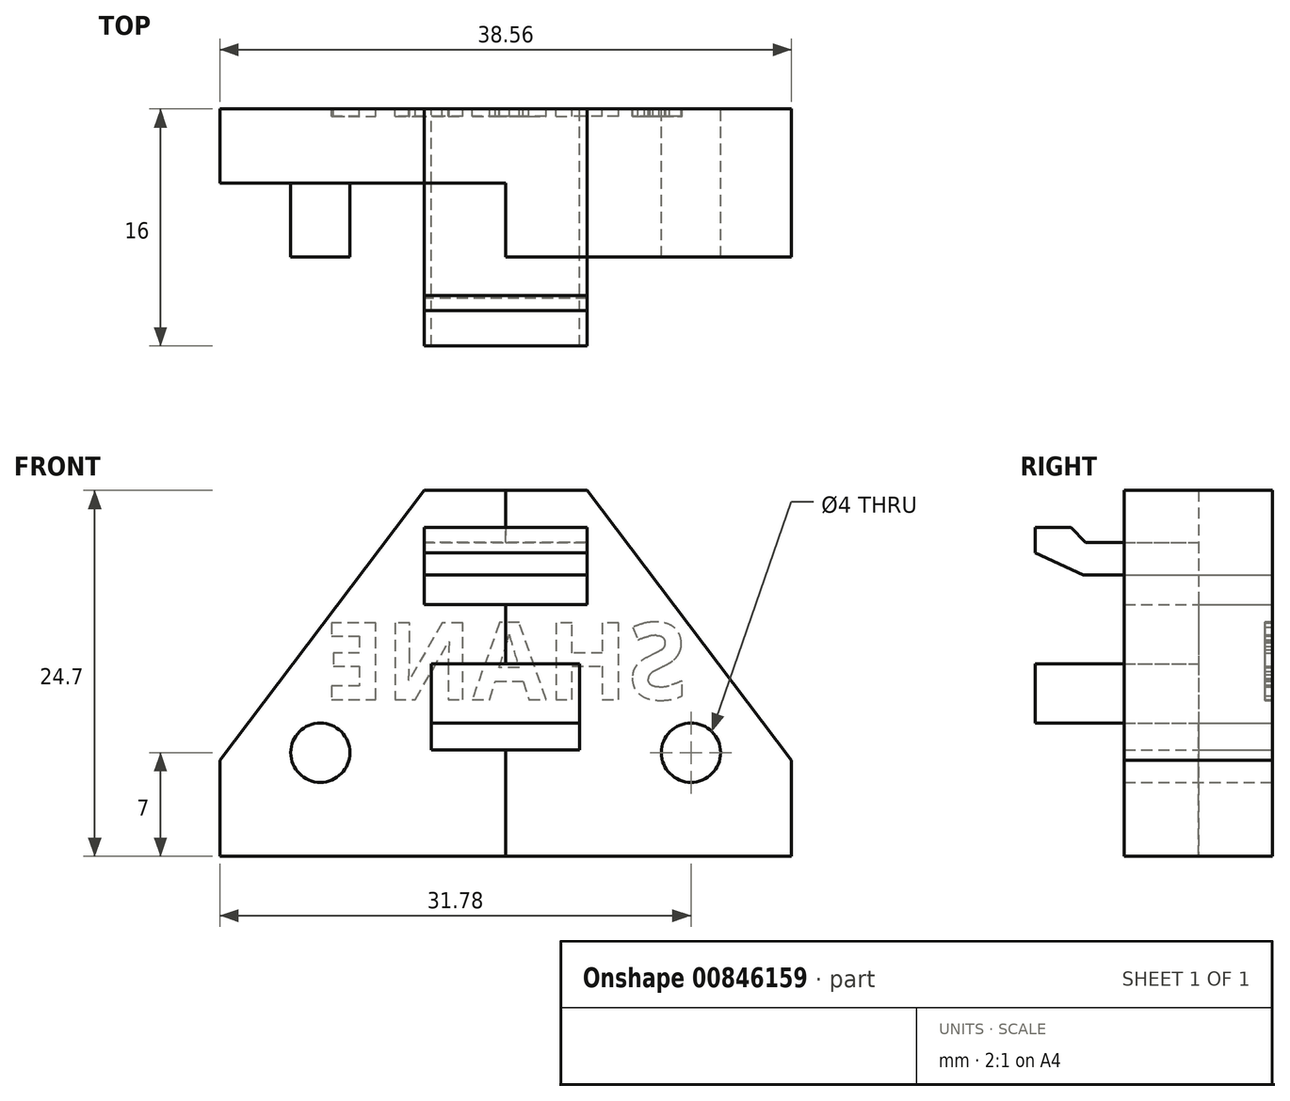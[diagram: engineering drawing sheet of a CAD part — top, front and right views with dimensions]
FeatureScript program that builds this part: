
annotation { "Feature Type Name" : "Feature", "Feature Type Description" : "" }
export const myFeature = defineFeature(function(context is Context, id is Id, definition is map)
    precondition{}
    {
        {
            var Q0;
            Q0=qCreatedBy(makeId("Front.planeOp"),FACE);
            var sketch = newSketch(context, id + "F0", { "sketchPlane" : qUnion([Q0])});
            skPoint(sketch, "E0", {"position": v(0, 0) * mm});
            skPoint(sketch, "E1", {"position": v(0, -2) * mm});
            skPoint(sketch, "E2", {"position": v(-12.5, -2) * mm});
            skLineSegment(sketch, "E3", {"start": v(0, 0) * mm, "end": v(0, 10) * mm, "construction": true});
            skCircle(sketch, "E4", {"center": v(-12.5, -2) * mm, "radius": 2 * mm});
            skLineSegment(sketch, "E5.bottom", {"start": v(-5, 0) * mm, "end": v(5, 0) * mm});
            skLineSegment(sketch, "E5.top", {"start": v(-5, 4) * mm, "end": v(5, 4) * mm});
            skLineSegment(sketch, "E5.left", {"start": v(-5, 0) * mm, "end": v(-5, 4) * mm});
            skLineSegment(sketch, "E5.right", {"start": v(5, 0) * mm, "end": v(5, 4) * mm});
            skPoint(sketch, "E5.middle", {"position": v(0, 2) * mm});
            skLineSegment(sketch, "E6.bottom", {"start": v(-5.5, 10) * mm, "end": v(5.5, 10) * mm});
            skLineSegment(sketch, "E6.top", {"start": v(-5.5, 12.2) * mm, "end": v(5.5, 12.2) * mm});
            skLineSegment(sketch, "E6.left", {"start": v(-5.5, 10) * mm, "end": v(-5.5, 12.2) * mm});
            skLineSegment(sketch, "E6.right", {"start": v(5.5, 10) * mm, "end": v(5.5, 12.2) * mm});
            skPoint(sketch, "E6.middle", {"position": v(0, 11.1) * mm});
            skLineSegment(sketch, "E7.top", {"start": v(-5, -1.8) * mm, "end": v(5, -1.8) * mm});
            skLineSegment(sketch, "E7.left", {"start": v(-5, 0) * mm, "end": v(-5, -1.8) * mm});
            skLineSegment(sketch, "E7.right", {"start": v(5, 0) * mm, "end": v(5, -1.8) * mm});
            skLineSegment(sketch, "E8.top", {"start": v(-5.5, 8) * mm, "end": v(5.5, 8) * mm});
            skLineSegment(sketch, "E8.left", {"start": v(-5.5, 10) * mm, "end": v(-5.5, 8) * mm});
            skLineSegment(sketch, "E8.right", {"start": v(5.5, 10) * mm, "end": v(5.5, 8) * mm});
            skLineSegment(sketch, "E9.bottom", {"start": v(0, -9) * mm, "end": v(-19.28, -9) * mm});
            skLineSegment(sketch, "E9.top", {"start": v(0, 15.7) * mm, "end": v(-19.28, 15.7) * mm});
            skLineSegment(sketch, "E9.left", {"start": v(0, -9) * mm, "end": v(0, 15.7) * mm});
            skLineSegment(sketch, "E9.right", {"start": v(-19.28, -9) * mm, "end": v(-19.28, 15.7) * mm});
            skLineSegment(sketch, "E10", {"start": v(-5.5, 15.7) * mm, "end": v(-19.28, -2.5) * mm});
            skCircle(sketch, "E11.MirrorC", {"center": v(12.5, -2) * mm, "radius": 2 * mm});
            skLineSegment(sketch, "E12.MirrorCS", {"start": v(5.5, 15.7) * mm, "end": v(19.28, -2.5) * mm});
            skLineSegment(sketch, "E13.MirrorCS", {"start": v(19.28, -9) * mm, "end": v(19.28, 15.7) * mm});
            skLineSegment(sketch, "E14.MirrorCS", {"start": v(0, -9) * mm, "end": v(19.28, -9) * mm});
            skLineSegment(sketch, "E15.MirrorCS", {"start": v(0, 15.7) * mm, "end": v(19.28, 15.7) * mm});
            skSolve(sketch);
        }
        {
            var Q0;
            Q0=makeQuery(id+"F0.imprint","IMPRINT",FACE,{"disambiguationData":[TD([[makeQuery(id+"F0.imprint","IMPRINT",EDGE,{"derivedFrom":sQuery(id+"F0.wireOp",EDGE,"E4")}),-1.0]])]});
            var Q1;
            {var subQ5=sQuery(id+"F0.wireOp",EDGE,"E5.right");Q1=makeQuery(id+"F0.imprint","IMPRINT",FACE,{"disambiguationData":[TD([[makeQuery(id+"F0.imprint","IMPRINT",EDGE,{"derivedFrom":subQ5}),-1.0]])]});}
            extrude(context, id + "F1", {"entities" : qUnion([Q0, Q1]), "depth" : 5 * mm, "offsetDistance" : 25 * mm});
        }
        {
            var Q0;
            Q0=makeQuery(id+"F0.imprint","IMPRINT",FACE,{"disambiguationData":[TD([[makeQuery(id+"F0.imprint","IMPRINT",EDGE,{"derivedFrom":sQuery(id+"F0.wireOp",EDGE,"E4")}),1.0]])]});
            var Q1;
            Q1=makeQuery(id+"F0.imprint","IMPRINT",FACE,{"disambiguationData":[TD([[makeQuery(id+"F0.imprint","IMPRINT",EDGE,{"derivedFrom":sQuery(id+"F0.wireOp",EDGE,"E11.MirrorC")}),-1.0]])]});
            extrude(context, id + "F2", {"entities" : qUnion([Q0, Q1]), "operationType" : NewBodyOperationType.ADD, "depth" : 10 * mm, "offsetDistance" : 25 * mm});
        }
        {
            var Q0;
            {var subQ0=sQuery(id+"F0.wireOp",EDGE,"E5.right");Q0=makeQuery(id+"F0.imprint","IMPRINT",FACE,{"disambiguationData":[TD([[makeQuery(id+"F0.imprint","IMPRINT",EDGE,{"derivedFrom":subQ0}),1.0]])]});}
            var Q1;
            {var subQ0=sQuery(id+"F0.wireOp",EDGE,"E5.left");Q1=makeQuery(id+"F0.imprint","IMPRINT",FACE,{"disambiguationData":[TD([[makeQuery(id+"F0.imprint","IMPRINT",EDGE,{"derivedFrom":subQ0}),-1.0]])]});}
            var Q2;
            {var subQ0=sQuery(id+"F0.wireOp",EDGE,"E6.left");Q2=makeQuery(id+"F0.imprint","IMPRINT",FACE,{"disambiguationData":[TD([[makeQuery(id+"F0.imprint","IMPRINT",EDGE,{"derivedFrom":subQ0}),-1.0]])]});}
            var Q3;
            {var subQ0=sQuery(id+"F0.wireOp",EDGE,"E6.right");Q3=makeQuery(id+"F0.imprint","IMPRINT",FACE,{"disambiguationData":[TD([[makeQuery(id+"F0.imprint","IMPRINT",EDGE,{"derivedFrom":subQ0}),1.0]])]});}
            extrude(context, id + "F3", {"entities" : qUnion([Q0, Q1, Q2, Q3]), "operationType" : NewBodyOperationType.ADD, "depth" : 16 * mm, "offsetDistance" : 25 * mm});
        }
        {
            var Q0;
            Q0=makeQuery(id+"F3.opExtrude","SWEPT_FACE",FACE,{"disambiguationData":[OSD([sQuery(id+"F0.wireOp",EDGE,"E6.top")])]});
            var sketch = newSketch(context, id + "F4", { "sketchPlane" : qUnion([Q0])});
            skLineSegment(sketch, "E16.bottom", {"start": v(5.5, -16) * mm, "end": v(-5.5, -16) * mm});
            skLineSegment(sketch, "E16.top", {"start": v(5.5, -12.6) * mm, "end": v(-5.5, -12.6) * mm});
            skLineSegment(sketch, "E16.left", {"start": v(5.5, -16) * mm, "end": v(5.5, -12.6) * mm});
            skLineSegment(sketch, "E16.right", {"start": v(-5.5, -16) * mm, "end": v(-5.5, -12.6) * mm});
            skSolve(sketch);
        }
        {
            var Q0;
            Q0 = qSketchRegion(id + "F4", true);
            extrude(context, id + "F5", {"entities" : qUnion([Q0]), "operationType" : NewBodyOperationType.ADD, "depth" : 1 * mm, "offsetDistance" : 25 * mm});
        }
        {
            var Q0;
            Q0=makeQuery(id+"F5.opExtrude","CAP_EDGE",EDGE,{"disambiguationData":[OSD([sQuery(id+"F4.wireOp",EDGE,"E16.top")])],"isStart":false});
            chamfer(context, id + "F6", {"entities" : qUnion([Q0]), "width" : 1 * mm, "tangentPropagation" : true});
        }
        {
            var Q0;
            Q0=makeQuery(id+"F3.opExtrude","CAP_EDGE",EDGE,{"disambiguationData":[OSD([sQuery(id+"F0.wireOp",EDGE,"E6.bottom")])],"isStart":false});
            chamfer(context, id + "F7", {"entities" : qUnion([Q0]), "chamferType" : ChamferType.OFFSET_ANGLE, "width" : 1.5 * mm, "oppositeDirection" : false, "angle" : 65 * degree, "tangentPropagation" : true});
        }
        {
            var Q0;
            {var subQ0=sQuery(id+"F0.wireOp",EDGE,"E6.right");var subQ1=sQuery(id+"F0.wireOp",EDGE,"E6.left");var subQ2=sQuery(id+"F0.wireOp",EDGE,"E6.top");var subQ3=sQuery(id+"F0.wireOp",EDGE,"E5.right");var subQ4=sQuery(id+"F0.wireOp",EDGE,"E5.left");var subQ5=sQuery(id+"F0.wireOp",EDGE,"E5.top");var subQ6=sQuery(id+"F0.wireOp",EDGE,"E11.MirrorC");var subQ7=sQuery(id+"F0.wireOp",EDGE,"E4");Q0=makeQuery(id+"F3.boolean.opBoolean","MERGE",FACE,{"derivedFrom":[makeQuery(id+"F2.boolean.opBoolean","MERGE",FACE,{"derivedFrom":[makeQuery(id+"F1.opExtrude","CAP_FACE",FACE,{"disambiguationData":[OSD([subQ7,subQ5,subQ4,subQ3,subQ2,subQ1,subQ0,sQuery(id+"F0.wireOp",EDGE,"E7.top"),sQuery(id+"F0.wireOp",EDGE,"E7.left"),sQuery(id+"F0.wireOp",EDGE,"E7.right"),sQuery(id+"F0.wireOp",EDGE,"E8.top"),sQuery(id+"F0.wireOp",EDGE,"E8.left"),sQuery(id+"F0.wireOp",EDGE,"E8.right"),sQuery(id+"F0.wireOp",EDGE,"E9.bottom"),sQuery(id+"F0.wireOp",EDGE,"E9.top"),sQuery(id+"F0.wireOp",EDGE,"E9.right"),sQuery(id+"F0.wireOp",EDGE,"E10"),subQ6,sQuery(id+"F0.wireOp",EDGE,"E12.MirrorCS"),sQuery(id+"F0.wireOp",EDGE,"E13.MirrorCS"),sQuery(id+"F0.wireOp",EDGE,"E14.MirrorCS"),sQuery(id+"F0.wireOp",EDGE,"E15.MirrorCS")])],"isStart":true}),makeQuery(id+"F2.opExtrude","CAP_FACE",FACE,{"disambiguationData":[OSD([subQ7])],"isStart":true}),makeQuery(id+"F2.opExtrude","CAP_FACE",FACE,{"disambiguationData":[OSD([subQ6])],"isStart":true})]}),makeQuery(id+"F3.opExtrude","CAP_FACE",FACE,{"disambiguationData":[OSD([subQ5,subQ4,subQ3,sQuery(id+"F0.wireOp",EDGE,"E5.bottom")])],"isStart":true}),makeQuery(id+"F3.opExtrude","CAP_FACE",FACE,{"disambiguationData":[OSD([subQ2,subQ1,subQ0,sQuery(id+"F0.wireOp",EDGE,"E6.bottom")])],"isStart":true})]});}
            var sketch = newSketch(context, id + "F8", { "sketchPlane" : qUnion([Q0])});
            skText(sketch, "E17", { "text": "SHANE", "fontName": "OpenSans-Bold.ttf"});
            const initialGuessF8  = {"E17": [-0.01224, 0.0016, 1, 0, 0.0052]};
            skSetInitialGuess(sketch, initialGuessF8);
            skSolve(sketch);
        }
        {
            var Q0;
            Q0 = qSketchRegion(id + "F8", true);
            extrude(context, id + "F9", {"entities" : qUnion([Q0]), "operationType" : NewBodyOperationType.REMOVE, "oppositeDirection" : true, "depth" : 0.5 * mm, "offsetDistance" : 25 * mm});
        }
    });
